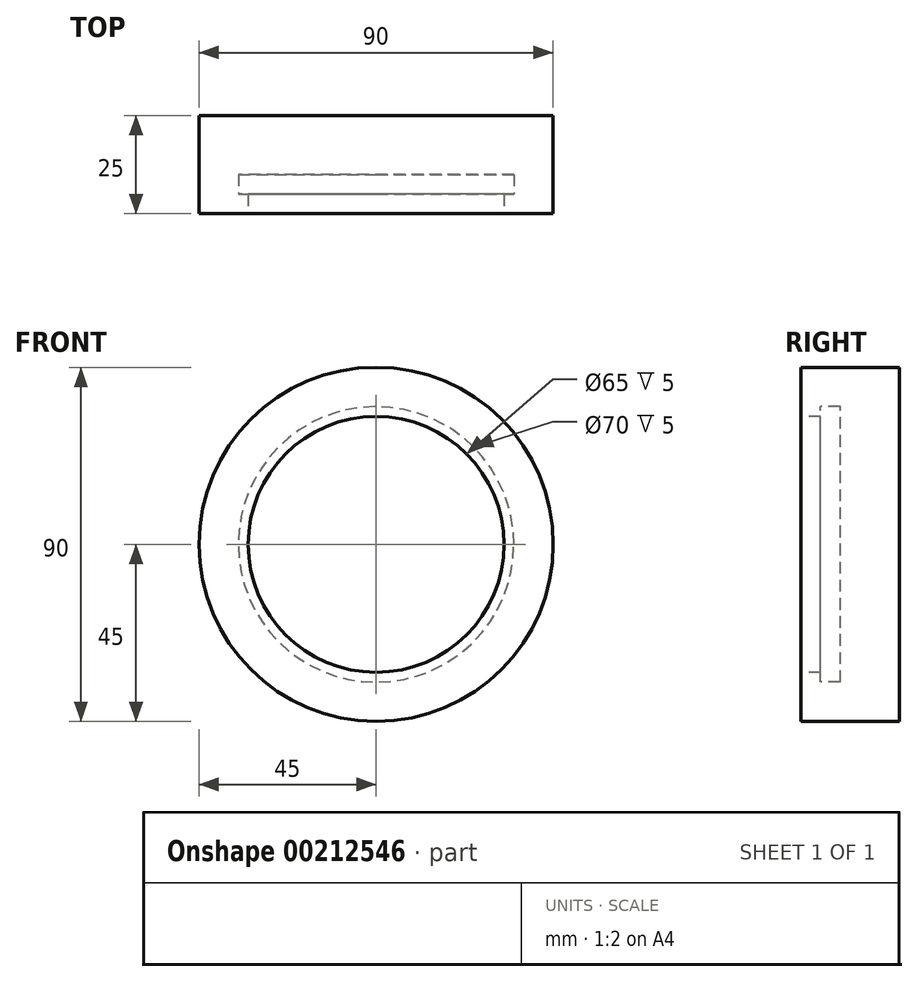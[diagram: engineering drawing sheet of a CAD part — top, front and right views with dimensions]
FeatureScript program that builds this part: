
annotation { "Feature Type Name" : "Feature", "Feature Type Description" : "" }
export const myFeature = defineFeature(function(context is Context, id is Id, definition is map)
    precondition{}
    {
        {
            var Q0;
            Q0=qCreatedBy(makeId("Front.planeOp"),FACE);
            var sketch = newSketch(context, id + "F0", { "sketchPlane" : qUnion([Q0])});
            skCircle(sketch, "E0", {"center": v(0, 0) * mm, "radius": 45 * mm});
            skSolve(sketch);
        }
        {
            var Q0;
            Q0 = qSketchRegion(id + "F0", true);
            extrude(context, id + "F1", {"entities" : qUnion([Q0]), "depth" : 25 * mm});
        }
        {
            var Q0;
            Q0=makeQuery(id+"F1.opExtrude","CAP_FACE",FACE,{"disambiguationData":[OSD([sQuery(id+"F0.wireOp",EDGE,"E0")])],"isStart":false});
            var sketch = newSketch(context, id + "F2", { "sketchPlane" : qUnion([Q0])});
            skCircle(sketch, "E1", {"center": v(0, 0) * mm, "radius": 32.5 * mm});
            skSolve(sketch);
        }
        {
            var Q0;
            Q0 = qSketchRegion(id + "F2", true);
            extrude(context, id + "F3", {"entities" : qUnion([Q0]), "operationType" : NewBodyOperationType.REMOVE, "oppositeDirection" : true, "depth" : 10 * mm});
        }
        {
            var Q0;
            Q0=makeQuery(id+"F1.opExtrude","CAP_FACE",FACE,{"disambiguationData":[OSD([sQuery(id+"F0.wireOp",EDGE,"E0")])],"isStart":false});
            cPlane(context, id + "F4", {"entities" : qUnion([Q0]), "cplaneType" : CPlaneType.OFFSET, "offset" : 5 * mm, "oppositeDirection" : true, "width" : 150 * mm, "height" : 150 * mm});
        }
        {
            var Q0;
            Q0=qCreatedBy(id+"F4.planeOp",FACE);
            var sketch = newSketch(context, id + "F5", { "sketchPlane" : qUnion([Q0])});
            skCircle(sketch, "E2", {"center": v(0, 0) * mm, "radius": 35 * mm});
            skCircle(sketch, "E3", {"center": v(0, 0) * mm, "radius": 32.5 * mm});
            skSolve(sketch);
        }
        {
            var Q0;
            Q0 = qSketchRegion(id + "F5", true);
            extrude(context, id + "F6", {"entities" : qUnion([Q0]), "operationType" : NewBodyOperationType.REMOVE, "oppositeDirection" : true, "depth" : 5 * mm});
        }
    });
